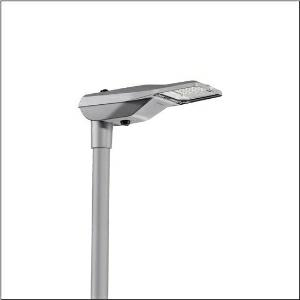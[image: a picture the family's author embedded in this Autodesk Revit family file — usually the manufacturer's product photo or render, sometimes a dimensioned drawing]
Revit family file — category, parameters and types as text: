
# Revit family: streetlight_sl_21_micro___st1_5a_5xe1p43t08db_e62a
name_source: partatom
category: Lighting Fixtures
units: mm (PartAtom-declared; Revit-internal decimal feet)

## family parameters
Cut with Voids When Loaded = No
Host = Face
Light Source = No
Part Type = Normal
Room Calculation Point = No
Round Connector Dimension = Use Diameter
Shared = No

## types (1)
- --- (1 x LED, 5230 lm, 39.1 W, 4000K)
    Apparent Load = 39 VA
    CIE Flux Codes = 22 53 95 100 100
    Color Rendering = 70
    Color Temperature = 4000K
    Default Elevation = 1800 mm
    Description = Streetlight SL 21 micro, mast luminaire, primary light control with lens, of PMMA, primary optical cover: cover, of toughened safety glass, transparent, light distribution: ST1.5a, light emission: direct distribution, primary light characteristic: asymmetric, installation type: side-entry, post-top, LED, High Power LED, rated luminous flux: 5.230lm, luminous efficacy: 134lm/W, light colour: 740, colour temperature: 4000K, control gear: D4i, control: flexible luminous flux parameterisation, time-dependent luminous flux control, constant luminous flux control, overheat protection, pre-setting: logarithmic dimming characteristic, mains connection: 220..240V, AC, 50/60Hz, start of lifetime: 39W, end of service life: 41W, reduction: 18W, luminaire housing, of diecast aluminium, powder-coated, SITECO metallic grey (DB 702S), corrosivity category C5 high according to DIN EN ISO 12944, please order mast flange separately, inclination adjustable: 0°, 5°, 10°, 15°, sealing non-destructively replaceable, multi-level sealing system, length: 528mm, width: 235mm, height: 110mm, mast flange for spigot size: 42mm (side-entry): 5XC10008XM4, 60/48mm (side-entry/post-top): 5XC10108XM2, 76/60mm (side-entry/post-top): 5XC10108XM1, Smart Interface below and above, protection rating (complete): IP66, insulation class (complete): insulation class II (safety insulation), certification: CE, ENEC, ENEC+, VDE, impact resistance: IK10, permissible operating ambient temperature for outdoor applications: -40..+50°C, standard-compliant lighting for roads and squares, packaging unit: 1 piece

Light Distribution: ST1.5a
    Height = 110 mm
    Lamp = 1 x LED
    Lamp Light Flux = 5230 lm
    Lamp Power = 39.1 W
    Lamp count = 1
    Length = 528 mm
    Luminous efficacy = 134 lm/W
    Manufacturer = Siteco
    ModVariant = No
    Model = 5XE1P43T08DB
    Number of Poles = 1
    OnlyDefault = Yes
    Power Factor = 1
    Product Name = Streetlight SL 21 micro | ST1.5a
    Product group = mast luminaire | pylon top
    ProductGroupID = 6100
    Protection Class = Protection class II
    Protection Degree = IP 66
    RLX_Detail_Level = 1
    RLX_Emergency_Light_Flux = 0 lm
    RLX_Emergency_Type = 0
    RLX_Emergency_Type_DB = No
    RlxData = <blob elided: 102865 chars, md5=f54f6b25>
    Socket = socket
    Standby Power = 0 W
    System Light Flux = 5230 lm
    System Power = 39 W
    Type Comments = factory setting: luminous flux: 100 % | dim-lin: 254 | 765 mA
    Type Image = l_1007239.jpg
    URL = http://relux.com
    VarID = @adj_153127
    Voltage = 0 V
    Weight = 0.00 kg
    Width = 235 mm

## geometry (parser evidence)
native form markers: Blend x4, Sweep x10
no freeform markers — native parametric forms only
